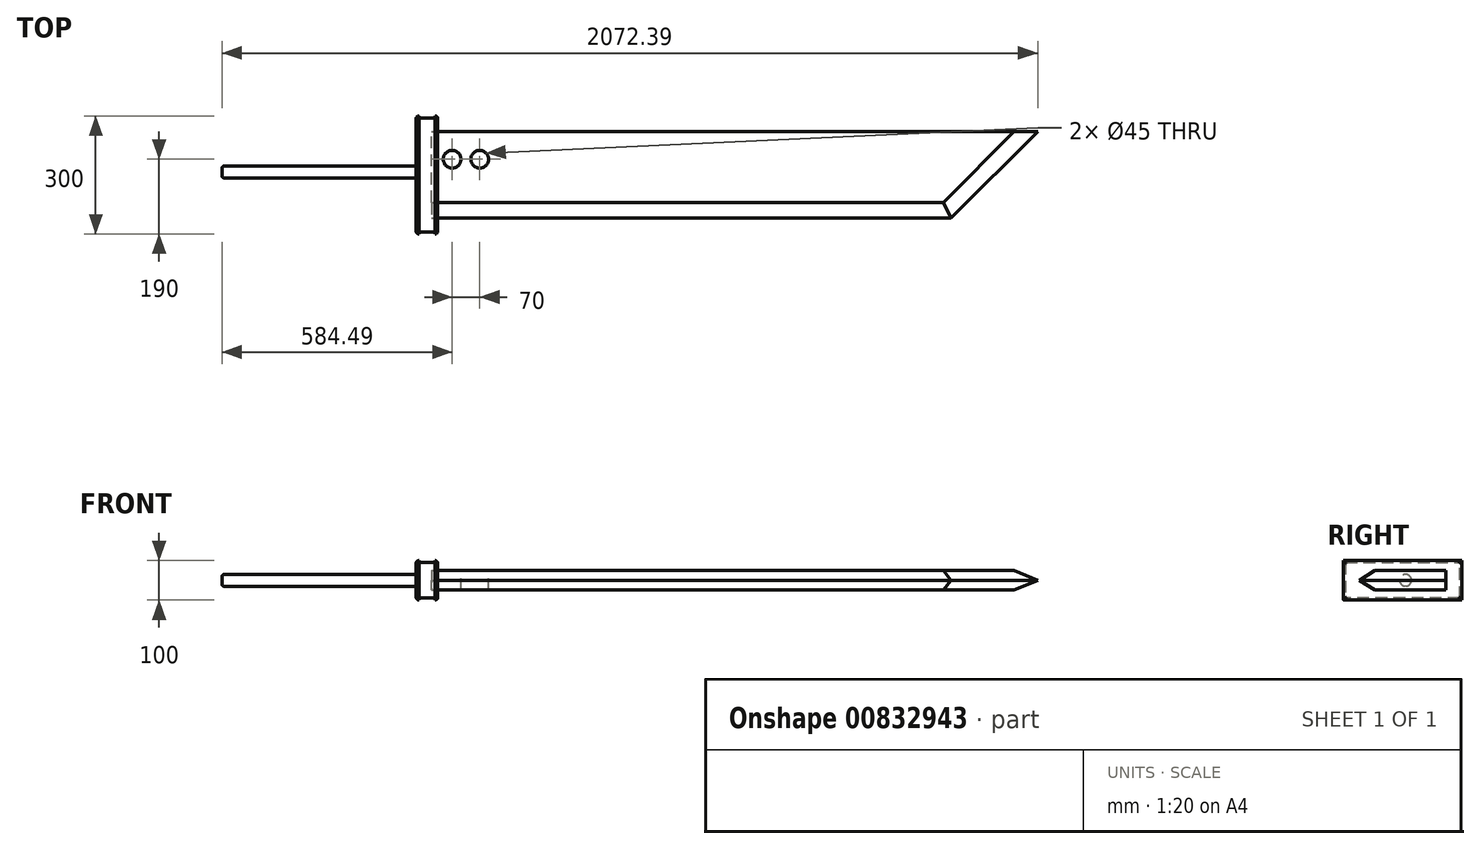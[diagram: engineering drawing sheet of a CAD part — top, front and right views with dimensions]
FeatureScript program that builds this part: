
annotation { "Feature Type Name" : "Feature", "Feature Type Description" : "" }
export const myFeature = defineFeature(function(context is Context, id is Id, definition is map)
    precondition{}
    {
        {
            var Q0;
            Q0=qCreatedBy(makeId("Top.planeOp"),FACE);
            var sketch = newSketch(context, id + "F0", { "sketchPlane" : qUnion([Q0])});
            skLineSegment(sketch, "E0", {"start": v(0, 0) * mm, "end": v(1600, 0) * mm});
            skLineSegment(sketch, "E1", {"start": v(1600, 0) * mm, "end": v(1300, -300) * mm});
            skLineSegment(sketch, "E2", {"start": v(1300, -300) * mm, "end": v(0, -300) * mm});
            skLineSegment(sketch, "E3", {"start": v(0, -300) * mm, "end": v(0, 0) * mm});
            skSolve(sketch);
        }
        {
            var Q0;
            Q0=makeQuery(id+"F0.imprint","IMPRINT",FACE,{"disambiguationData":[TD([[makeQuery(id+"F0.imprint","IMPRINT",EDGE,{"derivedFrom":sQuery(id+"F0.wireOp",EDGE,"E0")}),-1.0]])]});
            extrude(context, id + "F1", {"entities" : qUnion([Q0]), "depth" : 25 * mm, "offsetDistance" : 25 * mm});
        }
        {
            var Q0;
            Q0=makeQuery(id+"F1.opExtrude","CAP_EDGE",EDGE,{"disambiguationData":[OSD([sQuery(id+"F0.wireOp",EDGE,"E2")])],"isStart":false});
            chamfer(context, id + "F2", {"entities" : qUnion([Q0]), "chamferType" : ChamferType.TWO_OFFSETS, "width1" : 120 * mm, "oppositeDirection" : true, "width2" : 75 * mm, "tangentPropagation" : true});
        }
        {
            var Q0;
            Q0=makeQuery(id+"F1.opExtrude","CAP_EDGE",EDGE,{"disambiguationData":[OSD([sQuery(id+"F0.wireOp",EDGE,"E1")])],"isStart":false});
            chamfer(context, id + "F3", {"entities" : qUnion([Q0]), "chamferType" : ChamferType.TWO_OFFSETS, "width1" : 50 * mm, "oppositeDirection" : false, "width2" : 85 * mm, "tangentPropagation" : true});
        }
        {
            var Q0;
            Q0=makeQuery(id+"F1.opExtrude","SWEPT_BODY",BODY,{"disambiguationData":[OSD([sQuery(id+"F0.wireOp",EDGE,"E0"),sQuery(id+"F0.wireOp",EDGE,"E1"),sQuery(id+"F0.wireOp",EDGE,"E2"),sQuery(id+"F0.wireOp",EDGE,"E3")])]});
            var Q1;
            Q1=makeQuery(id+"F1.opExtrude","CAP_FACE",FACE,{"disambiguationData":[OSD([sQuery(id+"F0.wireOp",EDGE,"E0"),sQuery(id+"F0.wireOp",EDGE,"E1"),sQuery(id+"F0.wireOp",EDGE,"E2"),sQuery(id+"F0.wireOp",EDGE,"E3")])],"isStart":true});
            mirror(context, id + "F4", {"operationType" : NewBodyOperationType.ADD, "entities" : qUnion([Q0]), "mirrorPlane" : qUnion([Q1])});
        }
        {
            var Q0;
            Q0=makeQuery(id+"F1.opExtrude","CAP_FACE",FACE,{"disambiguationData":[OSD([sQuery(id+"F0.wireOp",EDGE,"E0"),sQuery(id+"F0.wireOp",EDGE,"E1"),sQuery(id+"F0.wireOp",EDGE,"E2"),sQuery(id+"F0.wireOp",EDGE,"E3")])],"isStart":false});
            var sketch = newSketch(context, id + "F5", { "sketchPlane" : qUnion([Q0])});
            skCircle(sketch, "E4", {"center": v(52, -70) * mm, "radius": 22.5 * mm});
            skCircle(sketch, "E5", {"center": v(122, -70) * mm, "radius": 22.5 * mm});
            skSolve(sketch);
        }
        {
            var Q0;
            Q0=makeQuery(id+"F5.imprint","IMPRINT",FACE,{"disambiguationData":[TD([[makeQuery(id+"F5.imprint","IMPRINT",EDGE,{"derivedFrom":sQuery(id+"F5.wireOp",EDGE,"E4")}),1.0]])]});
            var Q1;
            Q1=makeQuery(id+"F5.imprint","IMPRINT",FACE,{"disambiguationData":[TD([[makeQuery(id+"F5.imprint","IMPRINT",EDGE,{"derivedFrom":sQuery(id+"F5.wireOp",EDGE,"E5")}),1.0]])]});
            extrude(context, id + "F6", {"entities" : qUnion([Q0, Q1]), "operationType" : NewBodyOperationType.REMOVE, "oppositeDirection" : true, "depth" : 100 * mm, "offsetDistance" : 25 * mm});
        }
        {
            var Q0;
            Q0=qCreatedBy(makeId("Top.planeOp"),FACE);
            var sketch = newSketch(context, id + "F7", { "sketchPlane" : qUnion([Q0])});
            skLineSegment(sketch, "E6", {"start": v(15.5, 40) * mm, "end": v(-39.5, 40) * mm});
            skLineSegment(sketch, "E7", {"start": v(15.5, 40) * mm, "end": v(15.5, 40) * mm});
            skLineSegment(sketch, "E8", {"start": v(-39.5, 40) * mm, "end": v(-39.5, -260) * mm});
            skLineSegment(sketch, "E9", {"start": v(-39.5, -260) * mm, "end": v(15.5, -260) * mm});
            skLineSegment(sketch, "E10", {"start": v(15.5, -260) * mm, "end": v(15.5, -260) * mm});
            skLineSegment(sketch, "E11", {"start": v(15.5, -260) * mm, "end": v(15.5, 40) * mm});
            skSolve(sketch);
        }
        {
            var Q0;
            Q0 = qSketchRegion(id + "F7", true);
            extrude(context, id + "F8", {"entities" : qUnion([Q0]), "endBound" : BoundingType.SYMMETRIC, "depth" : 100 * mm, "offsetDistance" : 25 * mm});
        }
        {
            var Q0;
            Q0=makeQuery(id+"F8.opExtrude","CAP_EDGE",EDGE,{"disambiguationData":[OSD([sQuery(id+"F7.wireOp",EDGE,"E7"),sQuery(id+"F7.wireOp",EDGE,"E10"),sQuery(id+"F7.wireOp",EDGE,"E11")])],"isStart":false});
            var Q1;
            Q1=makeQuery(id+"F8.opExtrude","CAP_EDGE",EDGE,{"disambiguationData":[OSD([sQuery(id+"F7.wireOp",EDGE,"E7"),sQuery(id+"F7.wireOp",EDGE,"E10"),sQuery(id+"F7.wireOp",EDGE,"E11")])],"isStart":true});
            var Q2;
            Q2=makeQuery(id+"F8.opExtrude","CAP_EDGE",EDGE,{"disambiguationData":[OSD([sQuery(id+"F7.wireOp",EDGE,"E8")])],"isStart":false});
            var Q3;
            Q3=makeQuery(id+"F8.opExtrude","SWEPT_EDGE",EDGE,{"disambiguationData":[OSD([sQuery(id+"F7.wireOp",EDGE,"E8"),sQuery(id+"F7.wireOp",EDGE,"E9")])]});
            var Q4;
            Q4=makeQuery(id+"F8.opExtrude","SWEPT_EDGE",EDGE,{"disambiguationData":[OSD([sQuery(id+"F7.wireOp",EDGE,"E9"),sQuery(id+"F7.wireOp",EDGE,"E10")])]});
            var Q5;
            Q5=makeQuery(id+"F8.opExtrude","CAP_EDGE",EDGE,{"disambiguationData":[OSD([sQuery(id+"F7.wireOp",EDGE,"E8")])],"isStart":true});
            var Q6;
            Q6=makeQuery(id+"F8.opExtrude","SWEPT_EDGE",EDGE,{"disambiguationData":[OSD([sQuery(id+"F7.wireOp",EDGE,"E6"),sQuery(id+"F7.wireOp",EDGE,"E8")])]});
            var Q7;
            Q7=makeQuery(id+"F8.opExtrude","SWEPT_EDGE",EDGE,{"disambiguationData":[OSD([sQuery(id+"F7.wireOp",EDGE,"E6"),sQuery(id+"F7.wireOp",EDGE,"E7")])]});
            fillet(context, id + "F9", {"entities" : qUnion([Q0, Q1, Q2, Q3, Q4, Q5, Q6, Q7]), "radius" : 7 * mm, "tangentPropagation" : true, "allowEdgeOverflow" : false});
        }
        {
            var Q0;
            Q0=makeQuery(id+"F8.opExtrude","CAP_FACE",FACE,{"disambiguationData":[OSD([sQuery(id+"F7.wireOp",EDGE,"E6"),sQuery(id+"F7.wireOp",EDGE,"E7"),sQuery(id+"F7.wireOp",EDGE,"E8"),sQuery(id+"F7.wireOp",EDGE,"E9"),sQuery(id+"F7.wireOp",EDGE,"E10"),sQuery(id+"F7.wireOp",EDGE,"E11")])],"isStart":false});
            extrude(context, id + "F10", {"entities" : qUnion([Q0]), "operationType" : NewBodyOperationType.REMOVE, "oppositeDirection" : true, "depth" : 5 * mm, "offsetDistance" : 25 * mm});
        }
        {
            var Q0;
            Q0=makeQuery(id+"F8.opExtrude","SWEPT_FACE",FACE,{"disambiguationData":[OSD([sQuery(id+"F7.wireOp",EDGE,"E9")])]});
            extrude(context, id + "F11", {"entities" : qUnion([Q0]), "operationType" : NewBodyOperationType.REMOVE, "oppositeDirection" : true, "depth" : 5 * mm, "offsetDistance" : 25 * mm});
        }
        {
            var Q0;
            Q0=makeQuery(id+"F8.opExtrude","CAP_FACE",FACE,{"disambiguationData":[OSD([sQuery(id+"F7.wireOp",EDGE,"E6"),sQuery(id+"F7.wireOp",EDGE,"E7"),sQuery(id+"F7.wireOp",EDGE,"E8"),sQuery(id+"F7.wireOp",EDGE,"E9"),sQuery(id+"F7.wireOp",EDGE,"E10"),sQuery(id+"F7.wireOp",EDGE,"E11")])],"isStart":true});
            extrude(context, id + "F12", {"entities" : qUnion([Q0]), "operationType" : NewBodyOperationType.REMOVE, "oppositeDirection" : true, "depth" : 5 * mm, "offsetDistance" : 25 * mm});
        }
        {
            var Q0;
            Q0=makeQuery(id+"F8.opExtrude","SWEPT_FACE",FACE,{"disambiguationData":[OSD([sQuery(id+"F7.wireOp",EDGE,"E6")])]});
            extrude(context, id + "F13", {"entities" : qUnion([Q0]), "operationType" : NewBodyOperationType.REMOVE, "oppositeDirection" : true, "depth" : 5 * mm, "offsetDistance" : 25 * mm});
        }
        {
            var Q0;
            {var subQ0=sQuery(id+"F7.wireOp",EDGE,"E9");Q0=makeQuery(id+"F11.boolean.opBoolean","COPY",EDGE,{"derivedFrom":makeQuery(id+"F11.opExtrude","CAP_EDGE",EDGE,{"disambiguationData":[OSD([subQ0]),TDD([makeQuery(id+"F10.boolean.opBoolean","COPY",EDGE,{"derivedFrom":makeQuery(id+"F10.opExtrude","CAP_EDGE",EDGE,{"disambiguationData":[OSD([subQ0])],"isStart":false})})])],"isStart":false})});}
            var Q1;
            Q1=makeQuery(id+"F12.boolean.opBoolean","COPY",EDGE,{"derivedFrom":makeQuery(id+"F12.opExtrude","CAP_EDGE",EDGE,{"disambiguationData":[OSD([sQuery(id+"F7.wireOp",EDGE,"E9")])],"isStart":false})});
            var Q2;
            {var subQ0=sQuery(id+"F7.wireOp",EDGE,"E6");Q2=makeQuery(id+"F13.boolean.opBoolean","COPY",EDGE,{"derivedFrom":makeQuery(id+"F13.opExtrude","CAP_EDGE",EDGE,{"disambiguationData":[OSD([subQ0]),TDD([makeQuery(id+"F12.boolean.opBoolean","COPY",EDGE,{"derivedFrom":makeQuery(id+"F12.opExtrude","CAP_EDGE",EDGE,{"disambiguationData":[OSD([subQ0])],"isStart":false})})])],"isStart":false})});}
            var Q3;
            {var subQ0=sQuery(id+"F7.wireOp",EDGE,"E6");Q3=makeQuery(id+"F13.boolean.opBoolean","COPY",EDGE,{"derivedFrom":makeQuery(id+"F13.opExtrude","CAP_EDGE",EDGE,{"disambiguationData":[OSD([subQ0]),TDD([makeQuery(id+"F10.boolean.opBoolean","COPY",EDGE,{"derivedFrom":makeQuery(id+"F10.opExtrude","CAP_EDGE",EDGE,{"disambiguationData":[OSD([subQ0])],"isStart":false})})])],"isStart":false})});}
            fillet(context, id + "F14", {"entities" : qUnion([Q0, Q1, Q2, Q3]), "radius" : 5 * mm, "tangentPropagation" : true, "allowEdgeOverflow" : false});
        }
        {
            var Q0;
            Q0=qCreatedBy(makeId("Top.planeOp"),FACE);
            var sketch = newSketch(context, id + "F15", { "sketchPlane" : qUnion([Q0])});
            skLineSegment(sketch, "E12", {"start": v(-32.5, -117.53) * mm, "end": v(-532.5, -117.53) * mm});
            skLineSegment(sketch, "E13", {"start": v(-532.5, -117.53) * mm, "end": v(-532.5, -102.53) * mm});
            skLineSegment(sketch, "E14", {"start": v(-532.5, -102.53) * mm, "end": v(-32.5, -102.53) * mm});
            skLineSegment(sketch, "E15", {"start": v(-32.5, -102.53) * mm, "end": v(-32.5, -117.53) * mm});
            skSolve(sketch);
        }
        {
            var Q0;
            Q0=makeQuery(id+"F15.imprint","IMPRINT",FACE,{"disambiguationData":[TD([[makeQuery(id+"F15.imprint","IMPRINT",EDGE,{"derivedFrom":sQuery(id+"F15.wireOp",EDGE,"E12")}),-1.0]])]});
            var Q1;
            Q1=sQuery(id+"F15.wireOp",EDGE,"E14");
            revolve(context, id + "F16", {"operationType" : NewBodyOperationType.ADD, "surfaceOperationType" : NewSurfaceOperationType.NEW, "entities" : qUnion([Q0]), "axis" : qUnion([Q1]), "revolveType" : RevolveType.FULL});
        }
        {
            var Q0;
            Q0=makeQuery(id+"F16.opRevolve","SWEPT_EDGE",EDGE,{"disambiguationData":[OSD([sQuery(id+"F15.wireOp",EDGE,"E12"),sQuery(id+"F15.wireOp",EDGE,"E13")])]});
            fillet(context, id + "F17", {"entities" : qUnion([Q0]), "radius" : 5 * mm, "tangentPropagation" : true, "allowEdgeOverflow" : false});
        }
        {
            var Q0;
            Q0=makeQuery(id+"F16.boolean.opBoolean","INTERSECT",EDGE,{"derivedFrom":[makeQuery(id+"F8.opExtrude","SWEPT_FACE",FACE,{"disambiguationData":[OSD([sQuery(id+"F7.wireOp",EDGE,"E8")])]}),makeQuery(id+"F16.opRevolve","SWEPT_FACE",FACE,{"disambiguationData":[OSD([sQuery(id+"F15.wireOp",EDGE,"E12")])]})]});
            fillet(context, id + "F18", {"entities" : qUnion([Q0]), "radius" : 5 * mm, "tangentPropagation" : true, "allowEdgeOverflow" : false});
        }
        {
            var Q0;
            Q0=makeQuery(id+"F1.opExtrude","SWEPT_BODY",BODY,{"disambiguationData":[OSD([sQuery(id+"F0.wireOp",EDGE,"E0"),sQuery(id+"F0.wireOp",EDGE,"E1"),sQuery(id+"F0.wireOp",EDGE,"E2"),sQuery(id+"F0.wireOp",EDGE,"E3")])]});
            var Q1;
            Q1=makeQuery(id+"F8.opExtrude","SWEPT_BODY",BODY,{"disambiguationData":[OSD([sQuery(id+"F7.wireOp",EDGE,"E6"),sQuery(id+"F7.wireOp",EDGE,"E7"),sQuery(id+"F7.wireOp",EDGE,"E8"),sQuery(id+"F7.wireOp",EDGE,"E9"),sQuery(id+"F7.wireOp",EDGE,"E10"),sQuery(id+"F7.wireOp",EDGE,"E11")])]});
            booleanBodies(context, id + "F19", {"operationType" : BooleanOperationType.SUBTRACTION, "tools" : qUnion([Q0]), "targets" : qUnion([Q1]), "keepTools" : true});
        }
    });
